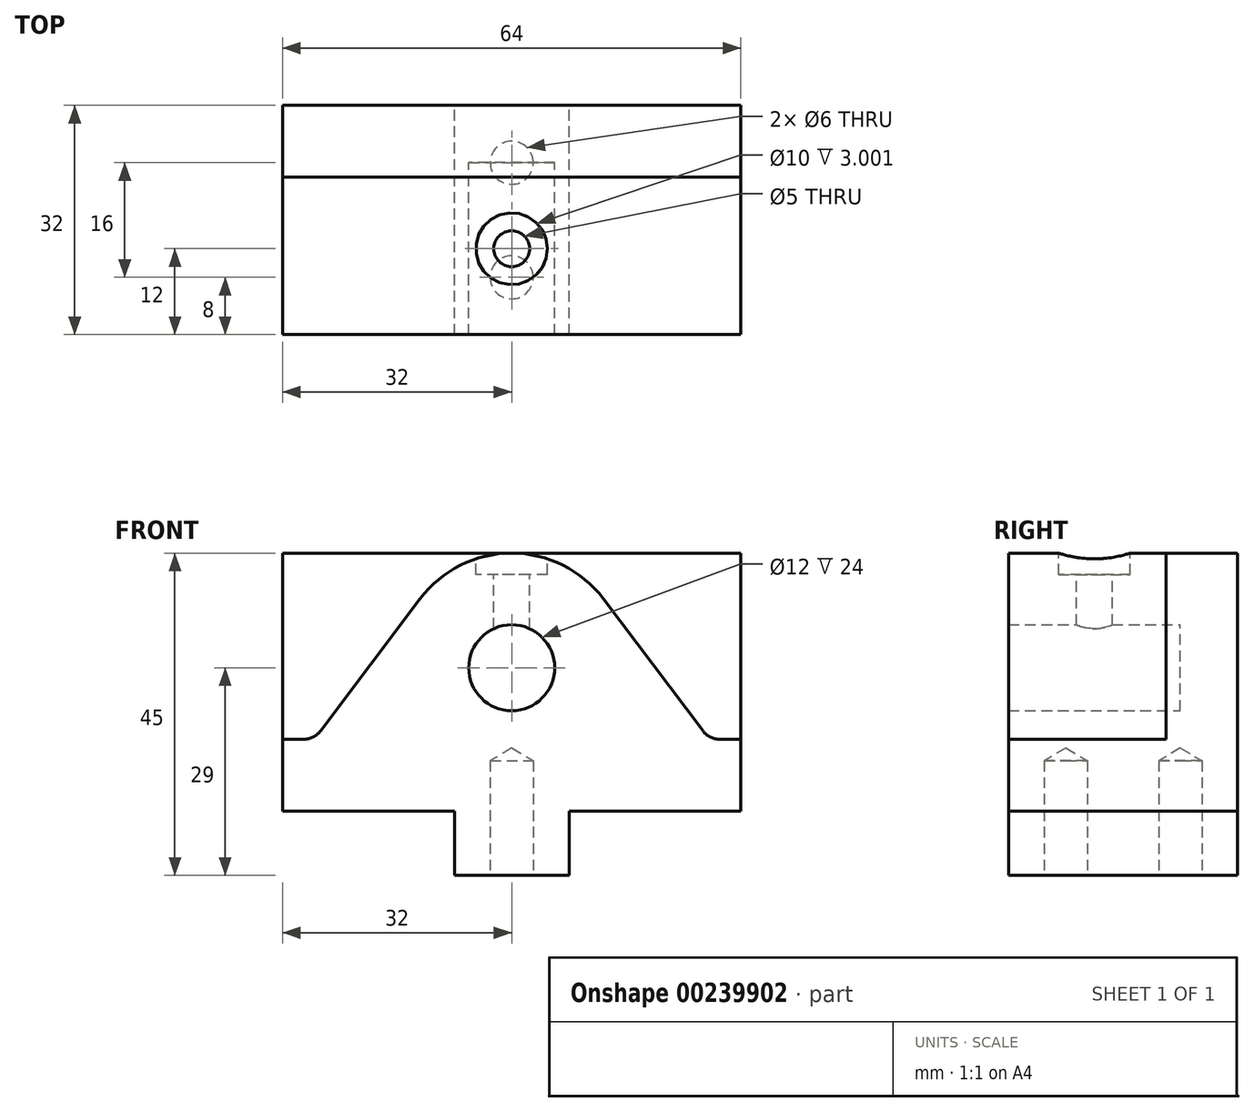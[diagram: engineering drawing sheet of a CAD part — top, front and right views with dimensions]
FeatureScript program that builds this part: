
annotation { "Feature Type Name" : "Feature", "Feature Type Description" : "" }
export const myFeature = defineFeature(function(context is Context, id is Id, definition is map)
    precondition{}
    {
        {
            var Q0;
            Q0=qCreatedBy(makeId("Front.planeOp"),FACE);
            var sketch = newSketch(context, id + "F0", { "sketchPlane" : qUnion([Q0])});
            skLineSegment(sketch, "E0.bottom", {"start": v(32, 18) * mm, "end": v(-32, 18) * mm});
            skLineSegment(sketch, "E0.top", {"start": v(32, -18) * mm, "end": v(8, -18) * mm});
            skLineSegment(sketch, "E0.left", {"start": v(32, 18) * mm, "end": v(32, -18) * mm});
            skLineSegment(sketch, "E0.right", {"start": v(-32, 18) * mm, "end": v(-32, -18) * mm});
            skPoint(sketch, "E0.middle", {"position": v(0, 0) * mm});
            skLineSegment(sketch, "E1", {"start": v(8, -18) * mm, "end": v(8, -27) * mm});
            skLineSegment(sketch, "E2", {"start": v(8, -27) * mm, "end": v(-8, -27) * mm});
            skLineSegment(sketch, "E3", {"start": v(-8, -27) * mm, "end": v(-8, -18) * mm});
            skPoint(sketch, "E4", {"position": v(0, -27) * mm});
            skLineSegment(sketch, "E5.trimOffspring", {"start": v(-8, -18) * mm, "end": v(-32, -18) * mm});
            skCircle(sketch, "E6", {"center": v(0, 2) * mm, "radius": 6 * mm});
            skArc(sketch, "E7", {"start": v(12.78, 11.63) * mm, "mid": v(0, 18) * mm, "end": v(-12.78, 11.63) * mm});
            skLineSegment(sketch, "E8", {"start": v(-32, -8) * mm, "end": v(-27.57, -8) * mm});
            skLineSegment(sketch, "E9", {"start": v(-27.57, -8) * mm, "end": v(-12.78, 11.63) * mm});
            skLineSegment(sketch, "E10", {"start": v(32, -8) * mm, "end": v(27.57, -8) * mm});
            skLineSegment(sketch, "E11", {"start": v(27.57, -8) * mm, "end": v(12.78, 11.63) * mm});
            skSolve(sketch);
        }
        {
            var Q0;
            {var subQ6=sQuery(id+"F0.wireOp",EDGE,"E0.top");Q0=makeQuery(id+"F0.imprint","IMPRINT",FACE,{"disambiguationData":[TD([[makeQuery(id+"F0.imprint","IMPRINT",EDGE,{"derivedFrom":subQ6}),-1.0]])]});}
            extrude(context, id + "F1", {"entities" : qUnion([Q0]), "depth" : 22 * mm});
        }
        {
            var Q0;
            Q0 = qSketchRegion(id + "F0", true);
            var Q1;
            Q1=makeQuery(id+"F0.imprint","IMPRINT",FACE,{"disambiguationData":[TD([[makeQuery(id+"F0.imprint","IMPRINT",EDGE,{"derivedFrom":sQuery(id+"F0.wireOp",EDGE,"E6")}),1.0]])]});
            extrude(context, id + "F2", {"entities" : qUnion([Q0, Q1]), "operationType" : NewBodyOperationType.ADD, "oppositeDirection" : true, "depth" : 10 * mm});
        }
        {
            var Q0;
            Q0=makeQuery(id+"F1.opExtrude","SWEPT_EDGE",EDGE,{"disambiguationData":[OSD([sQuery(id+"F0.wireOp",EDGE,"E8"),sQuery(id+"F0.wireOp",EDGE,"E9")])]});
            var Q1;
            Q1=makeQuery(id+"F1.opExtrude","SWEPT_EDGE",EDGE,{"disambiguationData":[OSD([sQuery(id+"F0.wireOp",EDGE,"E10"),sQuery(id+"F0.wireOp",EDGE,"E11")])]});
            fillet(context, id + "F3", {"entities" : qUnion([Q0, Q1]), "radius" : 3 * mm, "tangentPropagation" : true, "allowEdgeOverflow" : false});
        }
        {
            var Q0;
            Q0=makeQuery(id+"F2.opExtrude","SWEPT_FACE",FACE,{"disambiguationData":[OSD([sQuery(id+"F0.wireOp",EDGE,"E0.bottom")])]});
            var sketch = newSketch(context, id + "F4", { "sketchPlane" : qUnion([Q0])});
            skCircle(sketch, "E12", {"center": v(0, -10) * mm, "radius": 2.5 * mm});
            skSolve(sketch);
        }
        {
            var Q0;
            Q0=sQuery(id+"F4.wireOp",VERTEX,"E12.center");
            var Q1;
            Q1=makeQuery(id+"F1.opExtrude","SWEPT_BODY",BODY,{"disambiguationData":[OSD([sQuery(id+"F0.wireOp",EDGE,"E0.top"),sQuery(id+"F0.wireOp",EDGE,"E0.left"),sQuery(id+"F0.wireOp",EDGE,"E0.right"),sQuery(id+"F0.wireOp",EDGE,"E1"),sQuery(id+"F0.wireOp",EDGE,"E2"),sQuery(id+"F0.wireOp",EDGE,"E3"),sQuery(id+"F0.wireOp",EDGE,"E5.trimOffspring"),sQuery(id+"F0.wireOp",EDGE,"E6"),sQuery(id+"F0.wireOp",EDGE,"E7"),sQuery(id+"F0.wireOp",EDGE,"E8"),sQuery(id+"F0.wireOp",EDGE,"E9"),sQuery(id+"F0.wireOp",EDGE,"E10"),sQuery(id+"F0.wireOp",EDGE,"E11")])]});
            hole(context, id + "F5", {"style" : HoleStyle.C_BORE, "endStyle" : HoleEndStyle.BLIND, "holeDiameter" : 5 * mm, "cBoreDiameter" : 10 * mm, "cBoreDepth" : 3 * mm, "holeDepth" : 16 * mm, "startFromSketch" : true, "locations" : qUnion([Q0]), "scope" : qUnion([Q1])});
        }
        {
            var Q0;
            {var subQ0=sQuery(id+"F0.wireOp",EDGE,"E2");Q0=makeQuery(id+"F2.boolean.opBoolean","MERGE",FACE,{"derivedFrom":[makeQuery(id+"F1.opExtrude","SWEPT_FACE",FACE,{"disambiguationData":[OSD([subQ0])]}),makeQuery(id+"F2.opExtrude","SWEPT_FACE",FACE,{"disambiguationData":[OSD([subQ0])]})]});}
            var sketch = newSketch(context, id + "F6", { "sketchPlane" : qUnion([Q0])});
            skCircle(sketch, "E13", {"center": v(0, -2) * mm, "radius": 2.5 * mm});
            skCircle(sketch, "E14", {"center": v(0, 14) * mm, "radius": 2.5 * mm});
            skSolve(sketch);
        }
        {
            var Q0;
            Q0=makeQuery(id+"F0.imprint","IMPRINT",FACE,{"disambiguationData":[TD([[makeQuery(id+"F0.imprint","IMPRINT",EDGE,{"derivedFrom":sQuery(id+"F0.wireOp",EDGE,"E6")}),1.0]])]});
            extrude(context, id + "F7", {"entities" : qUnion([Q0]), "operationType" : NewBodyOperationType.REMOVE, "oppositeDirection" : true, "depth" : 2 * mm});
        }
        {
            var Q0;
            Q0=sQuery(id+"F6.wireOp",VERTEX,"E13.center");
            var Q1;
            Q1=sQuery(id+"F6.wireOp",VERTEX,"E14.center");
            var Q2;
            Q2=makeQuery(id+"F1.opExtrude","SWEPT_BODY",BODY,{"disambiguationData":[OSD([sQuery(id+"F0.wireOp",EDGE,"E0.top"),sQuery(id+"F0.wireOp",EDGE,"E0.left"),sQuery(id+"F0.wireOp",EDGE,"E0.right"),sQuery(id+"F0.wireOp",EDGE,"E1"),sQuery(id+"F0.wireOp",EDGE,"E2"),sQuery(id+"F0.wireOp",EDGE,"E3"),sQuery(id+"F0.wireOp",EDGE,"E5.trimOffspring"),sQuery(id+"F0.wireOp",EDGE,"E6"),sQuery(id+"F0.wireOp",EDGE,"E7"),sQuery(id+"F0.wireOp",EDGE,"E8"),sQuery(id+"F0.wireOp",EDGE,"E9"),sQuery(id+"F0.wireOp",EDGE,"E10"),sQuery(id+"F0.wireOp",EDGE,"E11")])]});
            hole(context, id + "F8", {"style" : HoleStyle.SIMPLE, "endStyle" : HoleEndStyle.BLIND, "holeDiameter" : 6 * mm, "holeDepth" : 16 * mm, "startFromSketch" : true, "locations" : qUnion([Q0, Q1]), "scope" : qUnion([Q2])});
        }
    });
